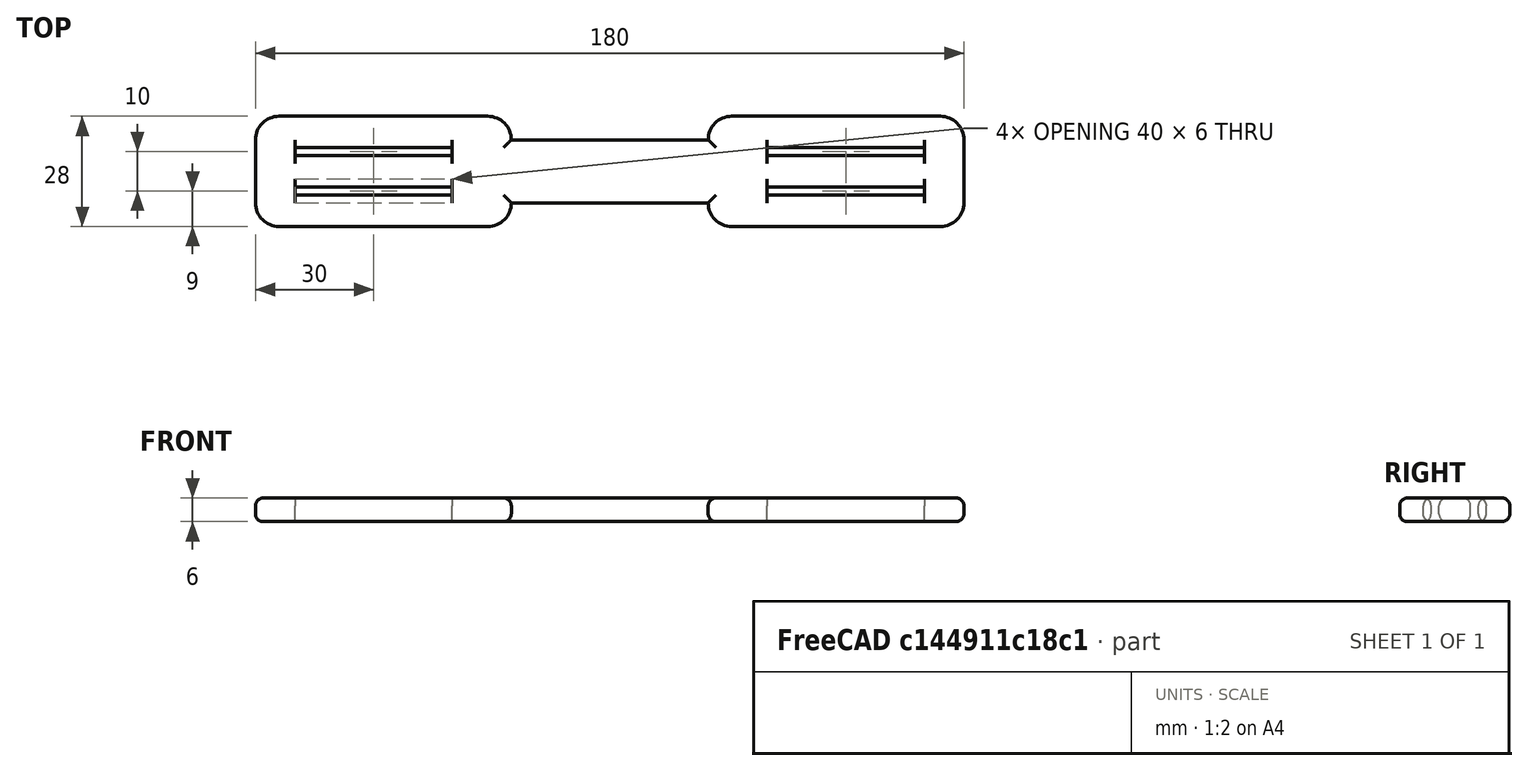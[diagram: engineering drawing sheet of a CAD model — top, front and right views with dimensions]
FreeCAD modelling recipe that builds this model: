
FCSTD DOCUMENT  (FreeCAD 0.18R4 (GitTag))
Label: Buckle Long 1_2
License: All rights reserved
LicenseURL: http://en.wikipedia.org/wiki/All_rights_reserved
objects: Part::Box×7, Part::Fillet×2, Part::MultiFuse×1, Part::Cut×1
note: 11 computed .brp shape members not serialized (recipe doc carries the construction recipe); baked Part::Feature solids carry a one-line shape summary decoded from their .brp

FEATURE [Part::Box] Box  label="Cube"
  AttacherType = Attacher::AttachEngine3D
  Height = 6
  Length = 180
  Placement = pos=(-110,-14,0) rot=(0,0,1;0rad)
  Width = 28
FEATURE [Part::Box] Box001  label="Cube001"
  AttacherType = Attacher::AttachEngine3D
  Height = 10
  Length = 40
  Placement = pos=(-100,-6,0) rot=(0,0,1;0rad)
  Width = 2
FEATURE [Part::Box] Box002  label="Cube002"
  AttacherType = Attacher::AttachEngine3D
  Height = 10
  Length = 40
  Placement = pos=(-100,4,0) rot=(0,0,1;0rad)
  Width = 2
FEATURE [Part::Box] Box003  label="Cube003"
  AttacherType = Attacher::AttachEngine3D
  Height = 10
  Length = 40
  Placement = pos=(20,-6,0) rot=(0,0,1;0rad)
  Width = 2
FEATURE [Part::Box] Box004  label="Cube004"
  AttacherType = Attacher::AttachEngine3D
  Height = 10
  Length = 40
  Placement = pos=(20,4,0) rot=(0,0,1;0rad)
  Width = 2
FEATURE [Part::Box] Box005  label="Cube005"
  AttacherType = Attacher::AttachEngine3D
  Height = 10
  Length = 50
  Placement = pos=(-45,-14,0) rot=(0,0,1;0rad)
  Width = 6
FEATURE [Part::Box] Box006  label="Cube006"
  AttacherType = Attacher::AttachEngine3D
  Height = 10
  Length = 50
  Placement = pos=(-45,8,0) rot=(0,0,1;0rad)
  Width = 6
FEATURE [Part::MultiFuse] Fusion  label="Holes"
  Refine = true
  Shapes = -> [Box001,Box003,Box004,Box002,Box005,Box006]
FEATURE [Part::Cut] Cut  label="Base"
  Base = -> Box
  Refine = true
  Tool = -> Fusion
FEATURE [Part::Fillet] Fillet
  Base = -> Cut
  Edges = 8 edges r=5.99: [Edge1,Edge3,Edge6,Edge35,Edge64,Edge65,Edge66,Edge67]
FEATURE [Part::Fillet] Fillet001
  Base = -> Fillet
  Edges = 48 edges r=2: [Edge1,Edge4,Edge5,Edge6,Edge7,Edge9,Edge10,Edge11,Edge13,Edge14,Edge16,Edge17,Edge18,Edge20,Edge21,Edge22,Edge23,Edge24,Edge26,Edge28,Edge30,Edge32,Edge34,Edge36,Edge38,Edge40,Edge42,Edge44,Edge45,Edge47,Edge48,Edge50,Edge51,Edge53,Edge54,Edge55,Edge57,Edge58,Edge59,Edge60,Edge62,Edge64,Edge66,+5 more]
